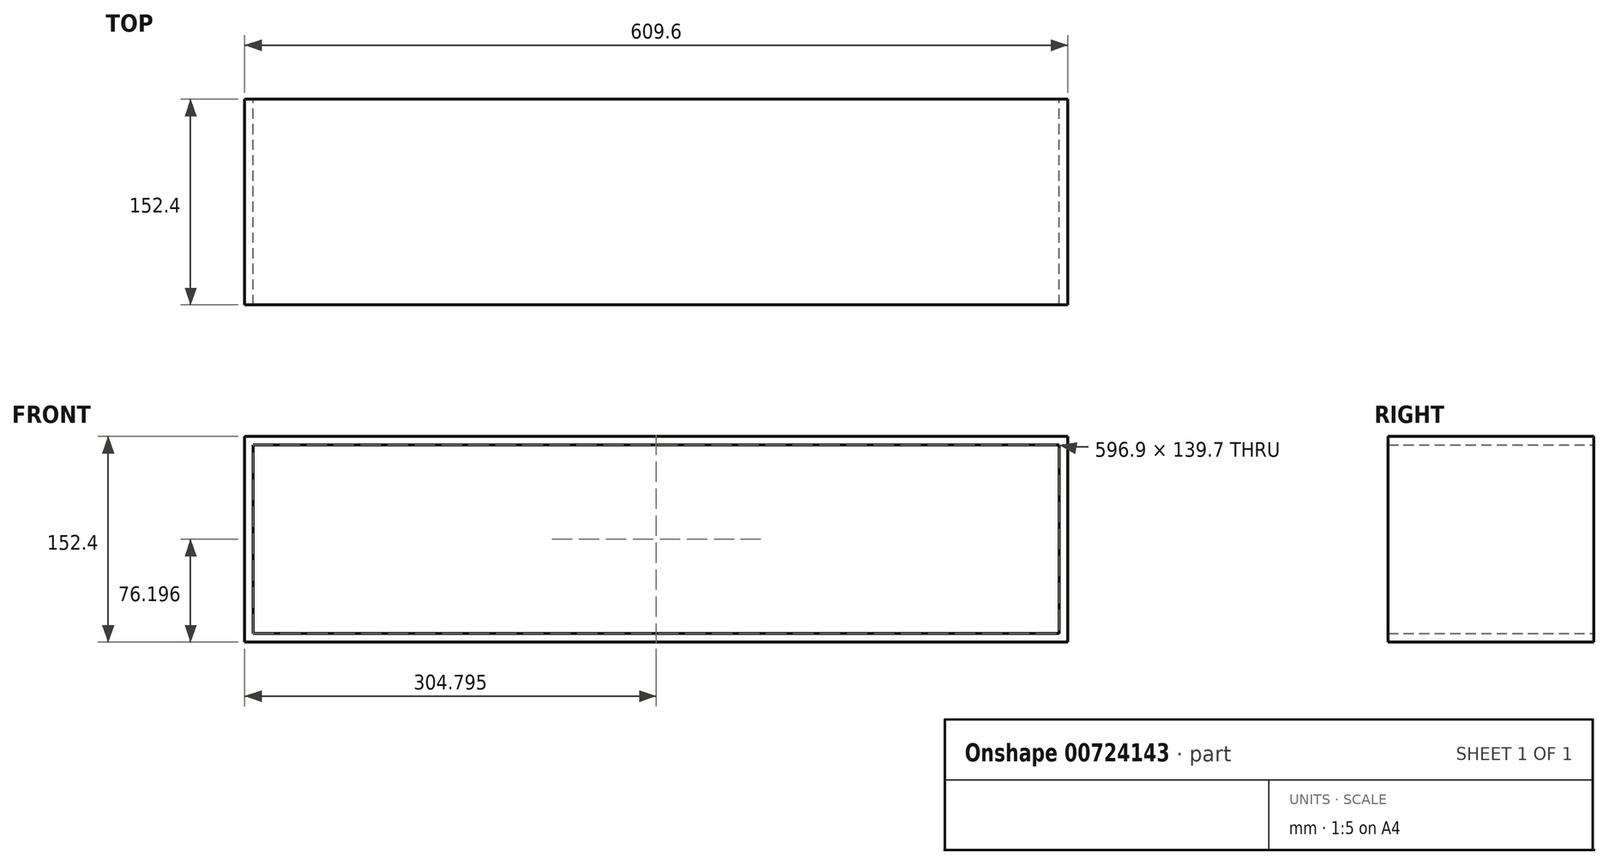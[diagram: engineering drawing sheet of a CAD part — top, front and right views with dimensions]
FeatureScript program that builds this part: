
annotation { "Feature Type Name" : "Feature", "Feature Type Description" : "" }
export const myFeature = defineFeature(function(context is Context, id is Id, definition is map)
    precondition{}
    {
        {
            var Q0;
            Q0=qCreatedBy(makeId("Front.planeOp"),FACE);
            var sketch = newSketch(context, id + "F0", { "sketchPlane" : qUnion([Q0])});
            skLineSegment(sketch, "E0.bottom", {"start": v(-299.8, -66.75) * mm, "end": v(309.8, -66.75) * mm});
            skLineSegment(sketch, "E0.top", {"start": v(-299.8, -219.15) * mm, "end": v(309.8, -219.15) * mm});
            skLineSegment(sketch, "E0.left", {"start": v(-299.8, -66.75) * mm, "end": v(-299.8, -219.15) * mm});
            skLineSegment(sketch, "E0.right", {"start": v(309.8, -66.75) * mm, "end": v(309.8, -219.15) * mm});
            skLineSegment(sketch, "E1.bottom", {"start": v(-293.45, -73.1) * mm, "end": v(303.45, -73.1) * mm});
            skLineSegment(sketch, "E1.top", {"start": v(-293.45, -212.8) * mm, "end": v(303.45, -212.8) * mm});
            skLineSegment(sketch, "E1.left", {"start": v(-293.45, -73.1) * mm, "end": v(-293.45, -212.8) * mm});
            skLineSegment(sketch, "E1.right", {"start": v(303.45, -73.1) * mm, "end": v(303.45, -212.8) * mm});
            skSolve(sketch);
        }
        {
            var Q0;
            Q0 = qSketchRegion(id + "F0", true);
            extrude(context, id + "F1", {"entities" : qUnion([Q0]), "depth" : 152.4 * mm, "offsetDistance" : 25.4 * mm});
        }
    });
